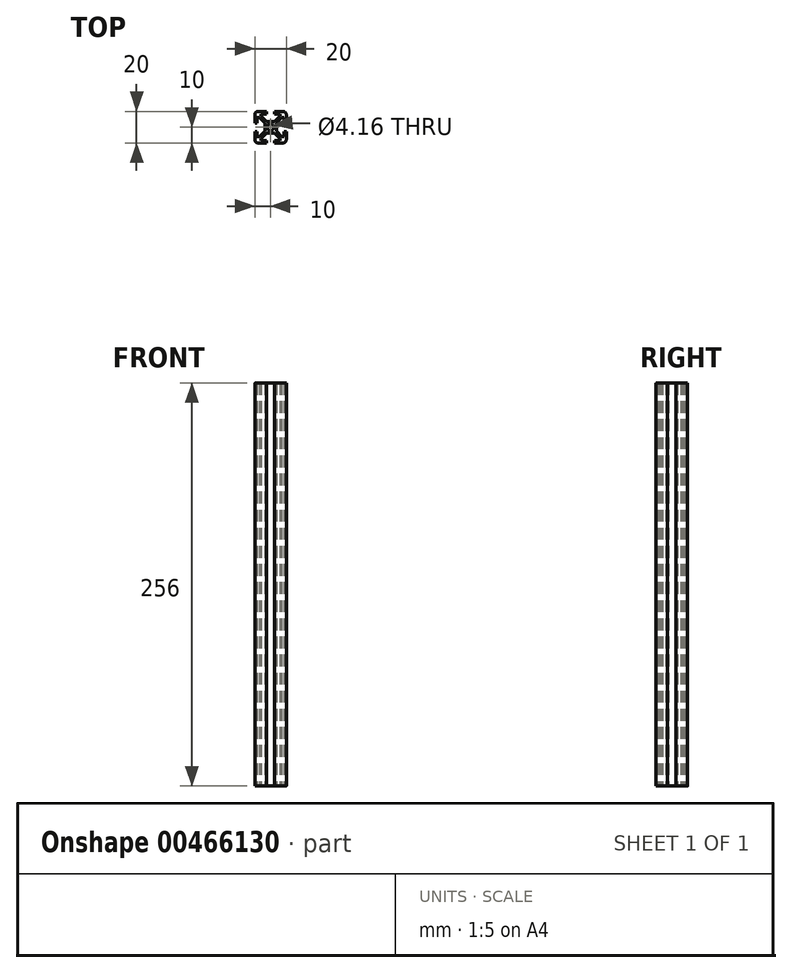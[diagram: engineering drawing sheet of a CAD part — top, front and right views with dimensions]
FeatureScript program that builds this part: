
annotation { "Feature Type Name" : "Feature", "Feature Type Description" : "" }
export const myFeature = defineFeature(function(context is Context, id is Id, definition is map)
    precondition{}
    {
        {
            var Q0;
            Q0=qCreatedBy(makeId("Top.planeOp"),FACE);
            var sketch = newSketch(context, id + "F0", { "sketchPlane" : qUnion([Q0])});
            skArc(sketch, "E0.filletArc", {"start": v(-8, 10) * mm, "mid": v(-9.41, 9.41) * mm, "end": v(-10, 8) * mm});
            skArc(sketch, "E1.filletArc", {"start": v(10, 8) * mm, "mid": v(9.41, 9.41) * mm, "end": v(8, 10) * mm});
            skArc(sketch, "E2.filletArc", {"start": v(8, -10) * mm, "mid": v(9.41, -9.41) * mm, "end": v(10, -8) * mm});
            skArc(sketch, "E3.filletArc", {"start": v(-10, -8) * mm, "mid": v(-9.41, -9.41) * mm, "end": v(-8, -10) * mm});
            skLineSegment(sketch, "E4", {"start": v(-2.63, 10) * mm, "end": v(-2.63, 8.5) * mm});
            skLineSegment(sketch, "E5", {"start": v(-2.63, 8.5) * mm, "end": v(-6, 8.5) * mm});
            skLineSegment(sketch, "E6", {"start": v(-6, 8.5) * mm, "end": v(-6, 7.06) * mm});
            skLineSegment(sketch, "E7", {"start": v(-6, 7.06) * mm, "end": v(-2.6, 3.66) * mm});
            skLineSegment(sketch, "E8", {"start": v(-10, 2.63) * mm, "end": v(-8.5, 2.63) * mm});
            skLineSegment(sketch, "E9", {"start": v(-8.5, 2.63) * mm, "end": v(-8.5, 6) * mm});
            skLineSegment(sketch, "E10", {"start": v(-8.5, 6) * mm, "end": v(-7.06, 6) * mm});
            skLineSegment(sketch, "E11", {"start": v(-7.06, 6) * mm, "end": v(-3.66, 2.6) * mm});
            skLineSegment(sketch, "E12.MirrorCS", {"start": v(8.5, 6) * mm, "end": v(7.06, 6) * mm});
            skLineSegment(sketch, "E13.MirrorCS", {"start": v(6, 8.5) * mm, "end": v(6, 7.06) * mm});
            skLineSegment(sketch, "E14.MirrorCS", {"start": v(10, 2.63) * mm, "end": v(8.5, 2.63) * mm});
            skLineSegment(sketch, "E15.MirrorCS", {"start": v(2.63, 10) * mm, "end": v(2.63, 8.5) * mm});
            skLineSegment(sketch, "E16.MirrorCS", {"start": v(7.06, 6) * mm, "end": v(3.66, 2.6) * mm});
            skLineSegment(sketch, "E17.MirrorCS", {"start": v(8.5, 2.63) * mm, "end": v(8.5, 6) * mm});
            skLineSegment(sketch, "E18.MirrorCS", {"start": v(2.63, 8.5) * mm, "end": v(6, 8.5) * mm});
            skLineSegment(sketch, "E19.MirrorCS", {"start": v(6, 7.06) * mm, "end": v(2.6, 3.66) * mm});
            skLineSegment(sketch, "E20.MirrorCS", {"start": v(-8.5, -6) * mm, "end": v(-7.06, -6) * mm});
            skLineSegment(sketch, "E21.MirrorCS", {"start": v(8.5, -6) * mm, "end": v(7.06, -6) * mm});
            skLineSegment(sketch, "E22.MirrorCS", {"start": v(2.63, -10) * mm, "end": v(2.63, -8.5) * mm});
            skLineSegment(sketch, "E23.MirrorCS", {"start": v(-2.63, -10) * mm, "end": v(-2.63, -8.5) * mm});
            skLineSegment(sketch, "E24.MirrorCS", {"start": v(10, -2.63) * mm, "end": v(8.5, -2.63) * mm});
            skLineSegment(sketch, "E25.MirrorCS", {"start": v(8.5, -2.63) * mm, "end": v(8.5, -6) * mm});
            skLineSegment(sketch, "E26.MirrorCS", {"start": v(-8.5, -2.63) * mm, "end": v(-8.5, -6) * mm});
            skLineSegment(sketch, "E27.MirrorCS", {"start": v(6, -8.5) * mm, "end": v(6, -7.06) * mm});
            skLineSegment(sketch, "E28.MirrorCS", {"start": v(-7.06, -6) * mm, "end": v(-3.66, -2.6) * mm});
            skLineSegment(sketch, "E29.MirrorCS", {"start": v(-10, -2.63) * mm, "end": v(-8.5, -2.63) * mm});
            skLineSegment(sketch, "E30.MirrorCS", {"start": v(6, -7.06) * mm, "end": v(2.6, -3.66) * mm});
            skLineSegment(sketch, "E31.MirrorCS", {"start": v(2.63, -8.5) * mm, "end": v(6, -8.5) * mm});
            skLineSegment(sketch, "E32.MirrorCS", {"start": v(-6, -8.5) * mm, "end": v(-6, -7.06) * mm});
            skLineSegment(sketch, "E33.MirrorCS", {"start": v(7.06, -6) * mm, "end": v(3.66, -2.6) * mm});
            skLineSegment(sketch, "E34.MirrorCS", {"start": v(-2.63, -8.5) * mm, "end": v(-6, -8.5) * mm});
            skLineSegment(sketch, "E35.MirrorCS", {"start": v(-6, -7.06) * mm, "end": v(-2.6, -3.66) * mm});
            skLineSegment(sketch, "E36", {"start": v(-2.6, 3.66) * mm, "end": v(2.6, 3.66) * mm});
            skLineSegment(sketch, "E37", {"start": v(3.66, 2.6) * mm, "end": v(3.66, -2.6) * mm});
            skLineSegment(sketch, "E38", {"start": v(2.6, -3.66) * mm, "end": v(-2.6, -3.66) * mm});
            skLineSegment(sketch, "E39", {"start": v(-3.66, -2.6) * mm, "end": v(-3.66, 2.6) * mm});
            skLineSegment(sketch, "E40", {"start": v(-8, 10) * mm, "end": v(-2.63, 10) * mm});
            skLineSegment(sketch, "E41", {"start": v(2.63, 10) * mm, "end": v(8, 10) * mm});
            skLineSegment(sketch, "E42", {"start": v(10, 8) * mm, "end": v(10, 2.63) * mm});
            skLineSegment(sketch, "E43", {"start": v(10, -2.63) * mm, "end": v(10, -8) * mm});
            skLineSegment(sketch, "E44", {"start": v(8, -10) * mm, "end": v(2.63, -10) * mm});
            skLineSegment(sketch, "E45", {"start": v(-2.63, -10) * mm, "end": v(-8, -10) * mm});
            skLineSegment(sketch, "E46", {"start": v(-10, -8) * mm, "end": v(-10, -2.63) * mm});
            skLineSegment(sketch, "E47", {"start": v(-10, 2.63) * mm, "end": v(-10, 8) * mm});
            skCircle(sketch, "E48", {"center": v(0, 0) * mm, "radius": 2.08 * mm});
            skSolve(sketch);
        }
        {
            var Q0;
            Q0=makeQuery(id+"F0.imprint","IMPRINT",FACE,{"disambiguationData":[TD([[makeQuery(id+"F0.imprint","IMPRINT",EDGE,{"derivedFrom":sQuery(id+"F0.wireOp",EDGE,"E0.filletArc")}),1.0]])]});
            extrude(context, id + "F1", {"entities" : qUnion([Q0]), "depth" : 128 * mm, "hasSecondDirection" : true, "secondDirectionOppositeDirection" : true, "secondDirectionDepth" : 128 * mm, "offsetDistance" : 25 * mm});
        }
    });
